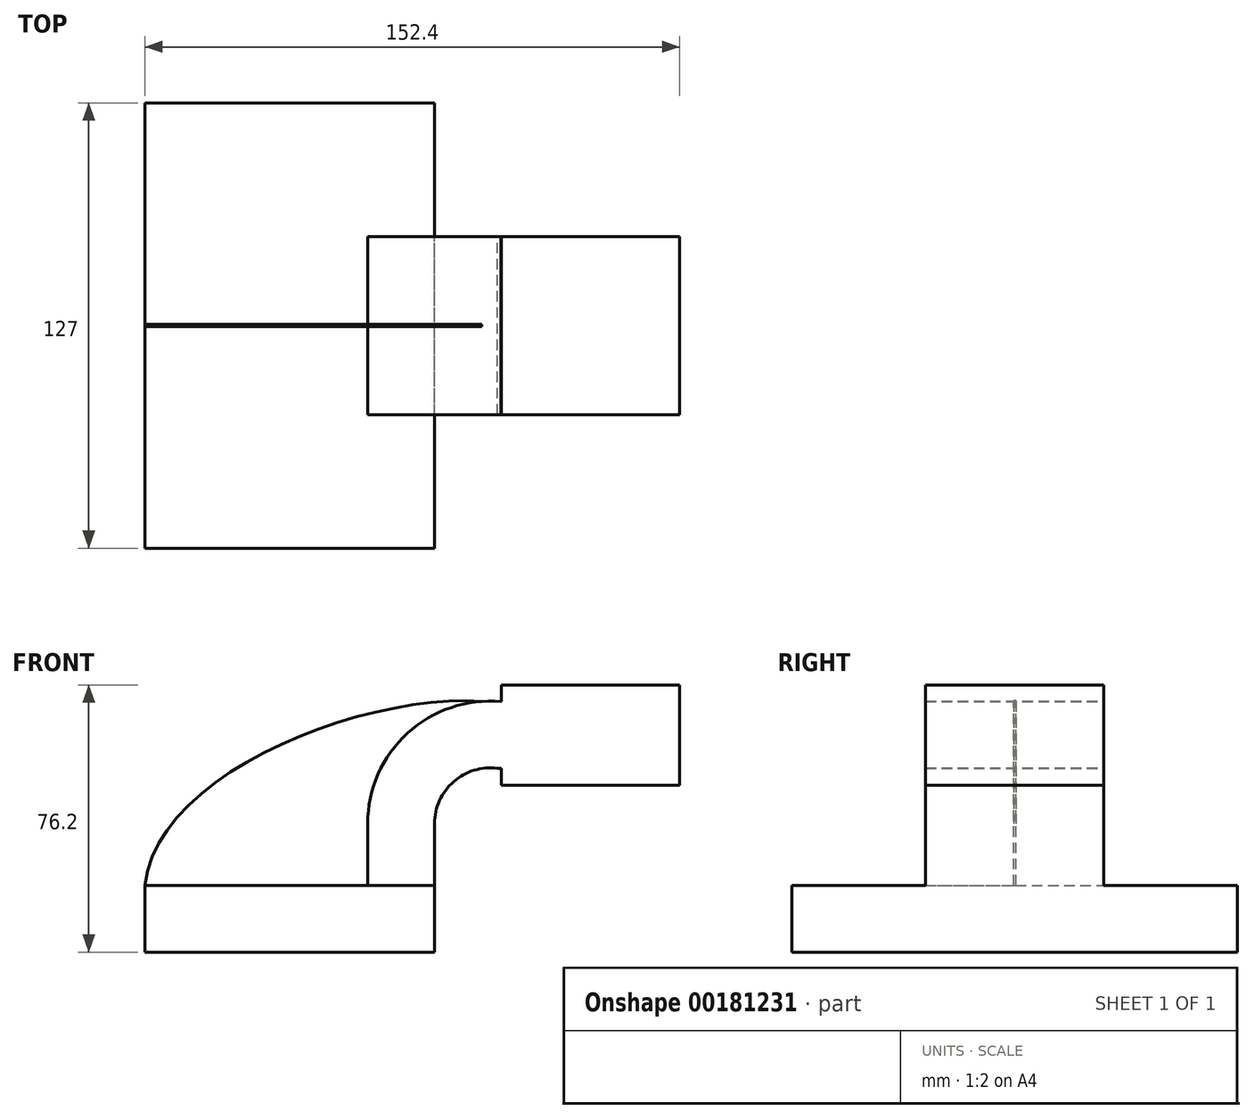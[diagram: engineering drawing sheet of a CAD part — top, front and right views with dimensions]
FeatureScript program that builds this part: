
annotation { "Feature Type Name" : "Feature", "Feature Type Description" : "" }
export const myFeature = defineFeature(function(context is Context, id is Id, definition is map)
    precondition{}
    {
        {
            var Q0;
            Q0=qCreatedBy(makeId("Front.planeOp"),FACE);
            var sketch = newSketch(context, id + "F0", { "sketchPlane" : qUnion([Q0])});
            skLineSegment(sketch, "E0.bottom", {"start": v(41.27, 9.53) * mm, "end": v(-41.28, 9.53) * mm});
            skLineSegment(sketch, "E0.top", {"start": v(41.28, -9.52) * mm, "end": v(-41.27, -9.52) * mm});
            skLineSegment(sketch, "E0.left", {"start": v(41.28, 9.53) * mm, "end": v(41.28, -9.52) * mm});
            skLineSegment(sketch, "E0.right", {"start": v(-41.28, 9.53) * mm, "end": v(-41.28, -9.52) * mm});
            skPoint(sketch, "E0.middle", {"position": v(0, 0) * mm});
            skLineSegment(sketch, "E1.bottom", {"start": v(111.12, 66.68) * mm, "end": v(60.32, 66.68) * mm});
            skLineSegment(sketch, "E1.top", {"start": v(111.12, 38.1) * mm, "end": v(60.32, 38.1) * mm});
            skLineSegment(sketch, "E1.left", {"start": v(111.12, 66.68) * mm, "end": v(111.12, 38.1) * mm});
            skLineSegment(sketch, "E1.right", {"start": v(60.32, 66.68) * mm, "end": v(60.32, 38.1) * mm});
            skPoint(sketch, "E1.middle", {"position": v(85.72, 52.39) * mm});
            skLineSegment(sketch, "E2", {"start": v(41.27, 9.53) * mm, "end": v(41.27, 27.13) * mm});
            skArc(sketch, "E3", {"start": v(41.27, 27.13) * mm, "mid": v(46.67, 39.06) * mm, "end": v(59.19, 42.88) * mm});
            skLineSegment(sketch, "E4", {"start": v(59.19, 42.88) * mm, "end": v(81.8, 42.88) * mm});
            skLineSegment(sketch, "E5.0", {"start": v(60.18, 61.93) * mm, "end": v(81.8, 61.93) * mm});
            skArc(sketch, "E5.1", {"start": v(22.22, 27.13) * mm, "mid": v(33.55, 52.88) * mm, "end": v(60.18, 61.93) * mm});
            skLineSegment(sketch, "E5.2", {"start": v(22.22, 9.53) * mm, "end": v(22.22, 27.13) * mm});
            skFitSpline(sketch, "E6", {"points": [v(-41.28, 9.53) * mm, v(54.7, 61.97) * mm], "startDerivative": vector(9.66, 95.77) * mm, "endDerivative": vector(102.37, -6.94) * mm});
            skSolve(sketch);
        }
        {
            var Q0;
            Q0=makeQuery(id+"F0.imprint","IMPRINT",FACE,{"disambiguationData":[TD([[makeQuery(id+"F0.imprint","IMPRINT",EDGE,{"derivedFrom":sQuery(id+"F0.wireOp",EDGE,"E0.top")}),-1.0]])]});
            extrude(context, id + "F1", {"entities" : qUnion([Q0]), "endBound" : BoundingType.SYMMETRIC, "depth" : 127 * mm});
        }
        {
            var Q0;
            {var subQ5=sQuery(id+"F0.wireOp",EDGE,"E2");Q0=makeQuery(id+"F0.imprint","IMPRINT",FACE,{"disambiguationData":[TD([[makeQuery(id+"F0.imprint","IMPRINT",EDGE,{"derivedFrom":subQ5}),1.0]])]});}
            var Q1;
            {var subQ1=sQuery(id+"F0.wireOp",EDGE,"E1.bottom");Q1=makeQuery(id+"F0.imprint","IMPRINT",FACE,{"disambiguationData":[TD([[makeQuery(id+"F0.imprint","IMPRINT",EDGE,{"derivedFrom":subQ1}),1.0]])]});}
            extrude(context, id + "F2", {"entities" : qUnion([Q0, Q1]), "operationType" : NewBodyOperationType.ADD, "endBound" : BoundingType.SYMMETRIC, "depth" : 50.8 * mm});
        }
        {
            var Q0;
            {var subQ2=sQuery(id+"F0.wireOp",EDGE,"E5.2");Q0=makeQuery(id+"F0.imprint","IMPRINT",FACE,{"disambiguationData":[TD([[makeQuery(id+"F0.imprint","IMPRINT",EDGE,{"derivedFrom":subQ2}),1.0]])]});}
            extrude(context, id + "F3", {"entities" : qUnion([Q0]), "operationType" : NewBodyOperationType.ADD, "endBound" : BoundingType.SYMMETRIC, "depth" : 0.64 * mm});
        }
    });
